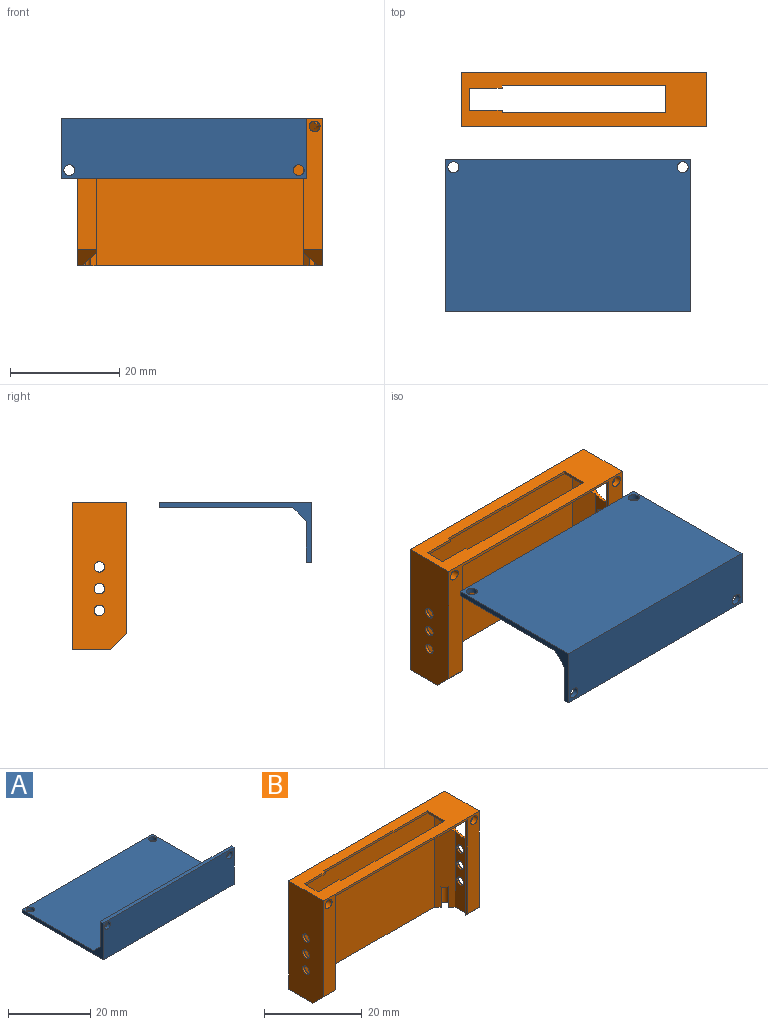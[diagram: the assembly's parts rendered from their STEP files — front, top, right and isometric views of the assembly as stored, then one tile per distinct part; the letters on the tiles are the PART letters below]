
ASSEMBLY  parts=2 mates=1
PART A: 13 faces, bbox 45x28x11 mm
  f0: plane 45x1mm, normal (0,1,0), area 45mm2, adj f1,f2,f3,f4
  f1: plane 28x11mm, normal (-1,0,0), area 41.1mm2, adj f0,f3,f4,f5,f6,f7,f8
  f2: plane 28x11mm, normal (1,0,0), area 41.1mm2, adj f0,f3,f4,f5,f6,f7,f8
  f3: plane 45x24.5mm, normal (0,0,1), area 1096.2mm2, adj f0,f1,f2,f8,f9,f10
  f4: plane 45x28mm, normal (0,0,-1), area 1253.7mm2, adj f0,f1,f2,f6,f9,f10
  f5: plane 45x7.5mm, normal (0,1,0), area 331.2mm2, adj f1,f2,f7,f8,f11,f12
  f6: plane 45x11mm, normal (0,-1,0), area 488.7mm2, adj f1,f2,f4,f7,f11,f12
  f7: plane 45x1mm, normal (0,0,1), area 45mm2, adj f1,f2,f5,f6
  f8: plane 45x2.5mm, normal (0,0.71,0.71), area 159.1mm2, adj f1,f2,f3,f5
  f9: cylinder r=1mm len=2mm, axis (0,0,-1), area 6.3mm2, adj f3,f4
  f10: cylinder r=1mm len=2mm, axis (0,0,-1), area 6.3mm2, adj f3,f4
  f11: cylinder r=1mm len=2mm, axis (0,-1,0), area 6.3mm2, adj f5,f6
  f12: cylinder r=1mm len=2mm, axis (0,-1,0), area 6.3mm2, adj f5,f6
PART B: 45 faces, bbox 45x10x27 mm
  f0: plane 1.03x1.03mm, normal (-0.71,0.71,0), area 0.4mm2, adj f11,f20,f21,f34
  f1: plane 2x0.54mm, normal (-1,0,0), area 0.3mm2, adj f20,f21,f24
  f2: plane 19.04x3mm, normal (-1,0,0), area 46.9mm2, adj f4,f21,f22,f24,f42,f43,f44
  f3: plane 45x10mm, normal (0,0,1), area 276mm2, adj f5,f6,f7,f8,f12,f13,f14,f15
  f4: plane 45x7mm, normal (0,0,-1), area 32.5mm2, adj f2,f5,f6,f8,f9,f10,f22,f24
  f5: plane 45x27mm, normal (0,1,0), area 1215mm2, adj f3,f4,f6,f8
  f6: plane 27x10mm, normal (-1,0,0), area 256.6mm2, adj f3,f4,f5,f7,f30,f39,f40,f41
  f7: plane 45x24mm, normal (0,-1,0), area 180.7mm2, adj f3,f6,f8,f20,f27,f28,f29,f30
  f8: plane 27x10mm, normal (1,0,0), area 206.3mm2, adj f3,f4,f5,f7,f21,f29,f42,f43
  f9: plane 38x26.5mm, normal (0,-1,0), area 1007mm2, adj f4,f20,f24,f25
  f10: plane 26.5x3mm, normal (1,0,0), area 70.6mm2, adj f4,f20,f25,f26,f39,f40,f41
  f11: plane 1x0.13mm, normal (-1,0,0), area 0mm2, adj f0,f20,f21
  f12: plane 0.5x0.5mm, normal (1,0,0), area 0.2mm2, adj f3,f13,f19,f20
  f13: plane 6x0.5mm, normal (0,1,0), area 3mm2, adj f3,f12,f14,f20
  f14: plane 4x0.5mm, normal (1,0,0), area 2mm2, adj f3,f13,f15,f20
  f15: plane 6x0.5mm, normal (0,-1,0), area 3mm2, adj f3,f14,f16,f20
  f16: plane 0.5x0.5mm, normal (1,0,0), area 0.3mm2, adj f3,f15,f17,f20
  f17: plane 30x0.5mm, normal (0,-1,0), area 15mm2, adj f3,f16,f18,f20
  f18: plane 5x0.5mm, normal (-1,0,0), area 2.5mm2, adj f3,f17,f19,f20
  f19: plane 30x0.5mm, normal (0,1,0), area 15mm2, adj f3,f12,f18,f20
  f20: plane 44x9.5mm, normal (0,0,-1), area 223mm2, adj f0,f1,f7,f9,f10,f11,f12,f13
  f21: cylinder r=4mm len=8mm, axis (1,0,0), area 40.9mm2, adj f0,f1,f2,f8,f11,f22,f23,f24
  f22: plane 22.5x3mm, normal (-0.71,0.71,0), area 78.9mm2, adj f2,f4,f21,f28,f29
  f23: plane 4x2mm, normal (-0.71,0.71,0), area 3.4mm2, adj f20,f21,f28,f33
  f24: plane 26.5x3mm, normal (-0.71,-0.71,0), area 91.5mm2, adj f1,f2,f4,f9,f20,f21,f37,f38
  f25: plane 26.5x3mm, normal (0.71,-0.71,0), area 105.4mm2, adj f4,f9,f10,f20,f35,f36
  f26: plane 26.5x3mm, normal (0.71,0.71,0), area 105.8mm2, adj f4,f10,f20,f27,f30,f31,f32
  f27: plane 24x0.5mm, normal (1,0,0), area 11.9mm2, adj f7,f20,f26,f30
  f28: plane 24x0.5mm, normal (-1,0,0), area 11.9mm2, adj f7,f20,f22,f23,f29
  f29: plane 3.5x3mm, normal (0,-0.71,-0.71), area 10.4mm2, adj f4,f7,f8,f22,f28
  f30: plane 3.5x3mm, normal (0,-0.71,-0.71), area 10.4mm2, adj f4,f6,f7,f26,f27
  f31: cylinder r=1mm len=2.5mm, axis (0,-1,0), area 13.7mm2, adj f7,f26,f32
  f32: plane 2x1mm, normal (0,-1,0), area 1.6mm2, adj f26,f31
  f33: cylinder r=1mm len=2.5mm, axis (0,-1,0), area 10.7mm2, adj f7,f21,f23,f34
  f34: plane 0.89x0.54mm, normal (0,-1,0), area 0.3mm2, adj f0,f21,f33
  f35: cylinder r=1mm len=5mm, axis (0,0,-1), area 23.6mm2, adj f4,f25,f36
  f36: plane 2x2mm, normal (0,0,-1), area 2.9mm2, adj f25,f35
  f37: cylinder r=1mm len=5mm, axis (0,0,-1), area 23.6mm2, adj f4,f24,f38
  f38: plane 2x2mm, normal (0,0,-1), area 2.9mm2, adj f24,f37
  f39: cylinder r=0.97mm len=1.95mm, axis (1,0,0), area 3.1mm2, adj f6,f10
  f40: cylinder r=0.97mm len=1.95mm, axis (1,0,0), area 3.1mm2, adj f6,f10
  f41: cylinder r=0.97mm len=1.95mm, axis (1,0,0), area 3.1mm2, adj f6,f10
  f42: cylinder r=0.97mm len=1.95mm, axis (1,0,0), area 3.1mm2, adj f2,f8
  f43: cylinder r=0.97mm len=1.95mm, axis (1,0,0), area 3.1mm2, adj f2,f8
  f44: cylinder r=0.97mm len=1.95mm, axis (1,0,0), area 3.1mm2, adj f2,f8
PLACE A rot(axis=(0,1,0),180deg) t=(-102.63,-57.55,40.3)mm
PLACE B t=(3.68,-19.95,13.3)mm
MATE fastened A.f4 <-> B.f3  axis (0,0,1) through (-37.4,-26.89,40.3)mm
